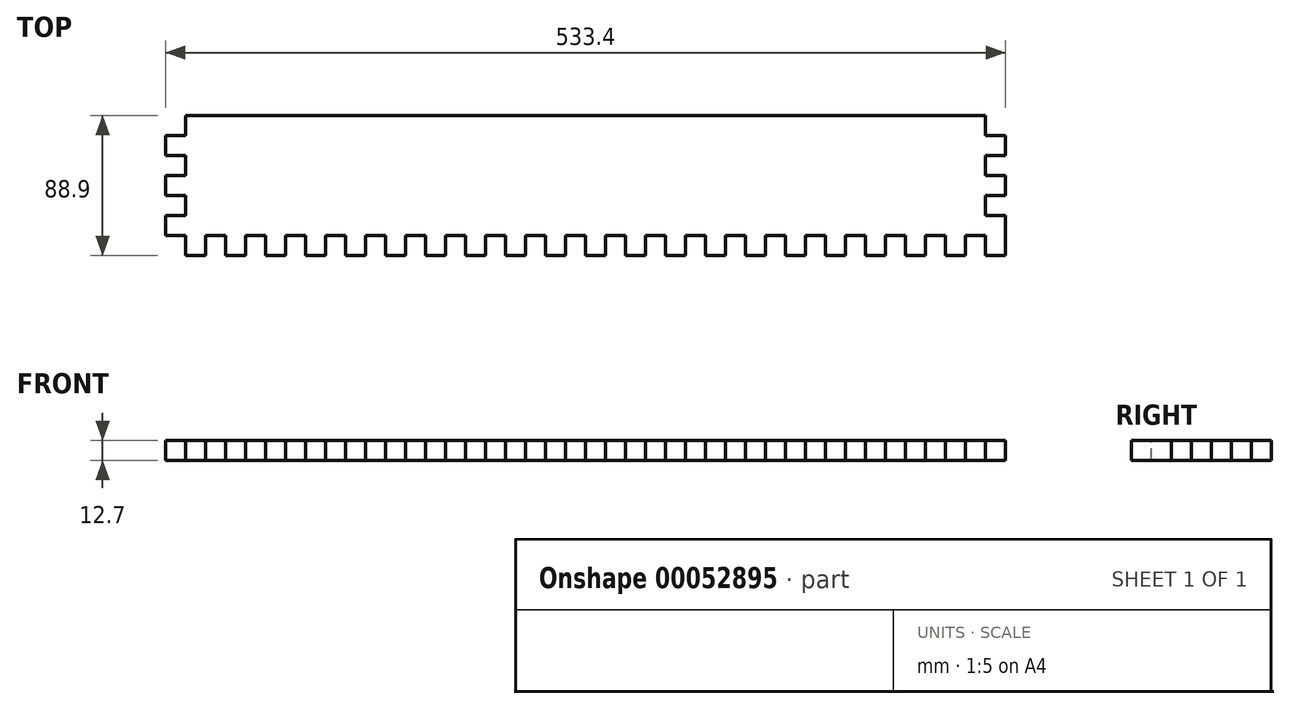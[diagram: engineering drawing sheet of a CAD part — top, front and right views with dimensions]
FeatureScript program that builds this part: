
annotation { "Feature Type Name" : "Feature", "Feature Type Description" : "" }
export const myFeature = defineFeature(function(context is Context, id is Id, definition is map)
    precondition{}
    {
        {
            var Q0;
            Q0=qCreatedBy(makeId("Top.planeOp"),FACE);
            var sketch = newSketch(context, id + "F0", { "sketchPlane" : qUnion([Q0])});
            skLineSegment(sketch, "E0.bottom", {"start": v(0, 0) * mm, "end": v(533.4, 0) * mm});
            skLineSegment(sketch, "E0.top", {"start": v(0, 88.9) * mm, "end": v(533.4, 88.9) * mm});
            skLineSegment(sketch, "E0.left", {"start": v(0, 0) * mm, "end": v(0, 88.9) * mm});
            skLineSegment(sketch, "E0.right", {"start": v(533.4, 0) * mm, "end": v(533.4, 88.9) * mm});
            skSolve(sketch);
        }
        {
            var Q0;
            Q0 = qSketchRegion(id + "F0", true);
            extrude(context, id + "F1", {"entities" : qUnion([Q0]), "depth" : 12.7 * mm});
        }
        {
            var Q0;
            Q0=makeQuery(id+"F1.opExtrude","CAP_FACE",FACE,{"disambiguationData":[OSD([sQuery(id+"F0.wireOp",EDGE,"E0.bottom"),sQuery(id+"F0.wireOp",EDGE,"E0.top"),sQuery(id+"F0.wireOp",EDGE,"E0.left"),sQuery(id+"F0.wireOp",EDGE,"E0.right")])],"isStart":false});
            var sketch = newSketch(context, id + "F2", { "sketchPlane" : qUnion([Q0])});
            skLineSegment(sketch, "E1.bottom", {"start": v(0, 0) * mm, "end": v(12.7, 0) * mm});
            skLineSegment(sketch, "E1.top", {"start": v(0, 12.7) * mm, "end": v(12.7, 12.7) * mm});
            skLineSegment(sketch, "E1.left", {"start": v(0, 0) * mm, "end": v(0, 12.7) * mm});
            skLineSegment(sketch, "E1.right", {"start": v(12.7, 0) * mm, "end": v(12.7, 12.7) * mm});
            skLineSegment(sketch, "E2.bottom", {"start": v(0, 25.4) * mm, "end": v(12.7, 25.4) * mm});
            skLineSegment(sketch, "E2.top", {"start": v(0, 38.1) * mm, "end": v(12.7, 38.1) * mm});
            skLineSegment(sketch, "E2.left", {"start": v(0, 25.4) * mm, "end": v(0, 38.1) * mm});
            skLineSegment(sketch, "E2.right", {"start": v(12.7, 25.4) * mm, "end": v(12.7, 38.1) * mm});
            skLineSegment(sketch, "E3.bottom", {"start": v(0, 76.2) * mm, "end": v(12.7, 76.2) * mm});
            skLineSegment(sketch, "E3.top", {"start": v(0, 88.9) * mm, "end": v(12.7, 88.9) * mm});
            skLineSegment(sketch, "E3.left", {"start": v(0, 76.2) * mm, "end": v(0, 88.9) * mm});
            skLineSegment(sketch, "E3.right", {"start": v(12.7, 76.2) * mm, "end": v(12.7, 88.9) * mm});
            skLineSegment(sketch, "E4.bottom", {"start": v(0, 50.8) * mm, "end": v(12.7, 50.8) * mm});
            skLineSegment(sketch, "E4.top", {"start": v(0, 63.5) * mm, "end": v(12.7, 63.5) * mm});
            skLineSegment(sketch, "E4.left", {"start": v(0, 50.8) * mm, "end": v(0, 63.5) * mm});
            skLineSegment(sketch, "E4.right", {"start": v(12.7, 50.8) * mm, "end": v(12.7, 63.5) * mm});
            skSolve(sketch);
        }
        {
            var Q0;
            Q0 = qSketchRegion(id + "F2", true);
            extrude(context, id + "F3", {"entities" : qUnion([Q0]), "operationType" : NewBodyOperationType.REMOVE, "oppositeDirection" : true, "depth" : 25.4 * mm});
        }
        {
            var Q0;
            Q0=makeQuery(id+"F1.opExtrude","CAP_FACE",FACE,{"disambiguationData":[OSD([sQuery(id+"F0.wireOp",EDGE,"E0.bottom"),sQuery(id+"F0.wireOp",EDGE,"E0.top"),sQuery(id+"F0.wireOp",EDGE,"E0.left"),sQuery(id+"F0.wireOp",EDGE,"E0.right")])],"isStart":false});
            var sketch = newSketch(context, id + "F4", { "sketchPlane" : qUnion([Q0])});
            skLineSegment(sketch, "E5.bottom", {"start": v(76.2, 0) * mm, "end": v(88.9, 0) * mm});
            skLineSegment(sketch, "E5.top", {"start": v(76.2, 12.7) * mm, "end": v(88.9, 12.7) * mm});
            skLineSegment(sketch, "E5.left", {"start": v(76.2, 0) * mm, "end": v(76.2, 12.7) * mm});
            skLineSegment(sketch, "E5.right", {"start": v(88.9, 0) * mm, "end": v(88.9, 12.7) * mm});
            skLineSegment(sketch, "E6.bottom", {"start": v(127, 0) * mm, "end": v(139.7, 0) * mm});
            skLineSegment(sketch, "E6.top", {"start": v(127, 12.7) * mm, "end": v(139.7, 12.7) * mm});
            skLineSegment(sketch, "E6.left", {"start": v(127, 0) * mm, "end": v(127, 12.7) * mm});
            skLineSegment(sketch, "E6.right", {"start": v(139.7, 0) * mm, "end": v(139.7, 12.7) * mm});
            skLineSegment(sketch, "E7.bottom", {"start": v(152.4, 0) * mm, "end": v(165.1, 0) * mm});
            skLineSegment(sketch, "E7.top", {"start": v(152.4, 12.7) * mm, "end": v(165.1, 12.7) * mm});
            skLineSegment(sketch, "E7.left", {"start": v(152.4, 0) * mm, "end": v(152.4, 12.7) * mm});
            skLineSegment(sketch, "E7.right", {"start": v(165.1, 0) * mm, "end": v(165.1, 12.7) * mm});
            skLineSegment(sketch, "E8.bottom", {"start": v(177.8, 0) * mm, "end": v(190.5, 0) * mm});
            skLineSegment(sketch, "E8.top", {"start": v(177.8, 12.7) * mm, "end": v(190.5, 12.7) * mm});
            skLineSegment(sketch, "E8.left", {"start": v(177.8, 0) * mm, "end": v(177.8, 12.7) * mm});
            skLineSegment(sketch, "E8.right", {"start": v(190.5, 0) * mm, "end": v(190.5, 12.7) * mm});
            skLineSegment(sketch, "E9.bottom", {"start": v(63.5, 0) * mm, "end": v(50.8, 0) * mm});
            skLineSegment(sketch, "E9.top", {"start": v(63.5, 12.7) * mm, "end": v(50.8, 12.7) * mm});
            skLineSegment(sketch, "E9.left", {"start": v(63.5, 0) * mm, "end": v(63.5, 12.7) * mm});
            skLineSegment(sketch, "E9.right", {"start": v(50.8, 0) * mm, "end": v(50.8, 12.7) * mm});
            skLineSegment(sketch, "E10.bottom", {"start": v(38.1, 0) * mm, "end": v(25.4, 0) * mm});
            skLineSegment(sketch, "E10.top", {"start": v(38.1, 12.7) * mm, "end": v(25.4, 12.7) * mm});
            skLineSegment(sketch, "E10.left", {"start": v(38.1, 0) * mm, "end": v(38.1, 12.7) * mm});
            skLineSegment(sketch, "E10.right", {"start": v(25.4, 0) * mm, "end": v(25.4, 12.7) * mm});
            skLineSegment(sketch, "E11.bottom", {"start": v(101.6, 0) * mm, "end": v(114.3, 0) * mm});
            skLineSegment(sketch, "E11.top", {"start": v(101.6, 12.7) * mm, "end": v(114.3, 12.7) * mm});
            skLineSegment(sketch, "E11.left", {"start": v(101.6, 0) * mm, "end": v(101.6, 12.7) * mm});
            skLineSegment(sketch, "E11.right", {"start": v(114.3, 0) * mm, "end": v(114.3, 12.7) * mm});
            skLineSegment(sketch, "E12.bottom", {"start": v(203.2, 0) * mm, "end": v(215.9, 0) * mm});
            skLineSegment(sketch, "E12.top", {"start": v(203.2, 12.7) * mm, "end": v(215.9, 12.7) * mm});
            skLineSegment(sketch, "E12.left", {"start": v(203.2, 0) * mm, "end": v(203.2, 12.7) * mm});
            skLineSegment(sketch, "E12.right", {"start": v(215.9, 0) * mm, "end": v(215.9, 12.7) * mm});
            skLineSegment(sketch, "E13.bottom", {"start": v(228.6, 0) * mm, "end": v(241.3, 0) * mm});
            skLineSegment(sketch, "E13.top", {"start": v(228.6, 12.7) * mm, "end": v(241.3, 12.7) * mm});
            skLineSegment(sketch, "E13.left", {"start": v(228.6, 0) * mm, "end": v(228.6, 12.7) * mm});
            skLineSegment(sketch, "E13.right", {"start": v(241.3, 0) * mm, "end": v(241.3, 12.7) * mm});
            skLineSegment(sketch, "E14.bottom", {"start": v(254, 0) * mm, "end": v(266.7, 0) * mm});
            skLineSegment(sketch, "E14.top", {"start": v(254, 12.7) * mm, "end": v(266.7, 12.7) * mm});
            skLineSegment(sketch, "E14.left", {"start": v(254, 0) * mm, "end": v(254, 12.7) * mm});
            skLineSegment(sketch, "E14.right", {"start": v(266.7, 0) * mm, "end": v(266.7, 12.7) * mm});
            skLineSegment(sketch, "E15.bottom", {"start": v(279.4, 0) * mm, "end": v(292.1, 0) * mm});
            skLineSegment(sketch, "E15.top", {"start": v(279.4, 12.7) * mm, "end": v(292.1, 12.7) * mm});
            skLineSegment(sketch, "E15.left", {"start": v(279.4, 0) * mm, "end": v(279.4, 12.7) * mm});
            skLineSegment(sketch, "E15.right", {"start": v(292.1, 0) * mm, "end": v(292.1, 12.7) * mm});
            skLineSegment(sketch, "E16.bottom", {"start": v(304.8, 0) * mm, "end": v(317.5, 0) * mm});
            skLineSegment(sketch, "E16.top", {"start": v(304.8, 12.7) * mm, "end": v(317.5, 12.7) * mm});
            skLineSegment(sketch, "E16.left", {"start": v(304.8, 0) * mm, "end": v(304.8, 12.7) * mm});
            skLineSegment(sketch, "E16.right", {"start": v(317.5, 0) * mm, "end": v(317.5, 12.7) * mm});
            skLineSegment(sketch, "E17.bottom", {"start": v(330.2, 0) * mm, "end": v(342.9, 0) * mm});
            skLineSegment(sketch, "E17.top", {"start": v(330.2, 12.7) * mm, "end": v(342.9, 12.7) * mm});
            skLineSegment(sketch, "E17.left", {"start": v(330.2, 0) * mm, "end": v(330.2, 12.7) * mm});
            skLineSegment(sketch, "E17.right", {"start": v(342.9, 0) * mm, "end": v(342.9, 12.7) * mm});
            skLineSegment(sketch, "E18.bottom", {"start": v(355.6, 0) * mm, "end": v(368.3, 0) * mm});
            skLineSegment(sketch, "E18.top", {"start": v(355.6, 12.7) * mm, "end": v(368.3, 12.7) * mm});
            skLineSegment(sketch, "E18.left", {"start": v(355.6, 0) * mm, "end": v(355.6, 12.7) * mm});
            skLineSegment(sketch, "E18.right", {"start": v(368.3, 0) * mm, "end": v(368.3, 12.7) * mm});
            skLineSegment(sketch, "E19.bottom", {"start": v(381, 0) * mm, "end": v(393.7, 0) * mm});
            skLineSegment(sketch, "E19.top", {"start": v(381, 12.7) * mm, "end": v(393.7, 12.7) * mm});
            skLineSegment(sketch, "E19.left", {"start": v(381, 0) * mm, "end": v(381, 12.7) * mm});
            skLineSegment(sketch, "E19.right", {"start": v(393.7, 0) * mm, "end": v(393.7, 12.7) * mm});
            skLineSegment(sketch, "E20.bottom", {"start": v(406.4, 0) * mm, "end": v(419.1, 0) * mm});
            skLineSegment(sketch, "E20.top", {"start": v(406.4, 12.7) * mm, "end": v(419.1, 12.7) * mm});
            skLineSegment(sketch, "E20.left", {"start": v(406.4, 0) * mm, "end": v(406.4, 12.7) * mm});
            skLineSegment(sketch, "E20.right", {"start": v(419.1, 0) * mm, "end": v(419.1, 12.7) * mm});
            skLineSegment(sketch, "E21.bottom", {"start": v(431.8, 0) * mm, "end": v(444.5, 0) * mm});
            skLineSegment(sketch, "E21.top", {"start": v(431.8, 12.7) * mm, "end": v(444.5, 12.7) * mm});
            skLineSegment(sketch, "E21.left", {"start": v(431.8, 0) * mm, "end": v(431.8, 12.7) * mm});
            skLineSegment(sketch, "E21.right", {"start": v(444.5, 0) * mm, "end": v(444.5, 12.7) * mm});
            skLineSegment(sketch, "E22.bottom", {"start": v(457.2, 0) * mm, "end": v(469.9, 0) * mm});
            skLineSegment(sketch, "E22.top", {"start": v(457.2, 12.7) * mm, "end": v(469.9, 12.7) * mm});
            skLineSegment(sketch, "E22.left", {"start": v(457.2, 0) * mm, "end": v(457.2, 12.7) * mm});
            skLineSegment(sketch, "E22.right", {"start": v(469.9, 0) * mm, "end": v(469.9, 12.7) * mm});
            skLineSegment(sketch, "E23.bottom", {"start": v(482.6, 0) * mm, "end": v(495.3, 0) * mm});
            skLineSegment(sketch, "E23.top", {"start": v(482.6, 12.7) * mm, "end": v(495.3, 12.7) * mm});
            skLineSegment(sketch, "E23.left", {"start": v(482.6, 0) * mm, "end": v(482.6, 12.7) * mm});
            skLineSegment(sketch, "E23.right", {"start": v(495.3, 0) * mm, "end": v(495.3, 12.7) * mm});
            skLineSegment(sketch, "E24.bottom", {"start": v(508, 0) * mm, "end": v(520.7, 0) * mm});
            skLineSegment(sketch, "E24.top", {"start": v(508, 12.7) * mm, "end": v(520.7, 12.7) * mm});
            skLineSegment(sketch, "E24.left", {"start": v(508, 0) * mm, "end": v(508, 12.7) * mm});
            skLineSegment(sketch, "E24.right", {"start": v(520.7, 0) * mm, "end": v(520.7, 12.7) * mm});
            skSolve(sketch);
        }
        {
            var Q0;
            Q0 = qSketchRegion(id + "F4", true);
            extrude(context, id + "F5", {"entities" : qUnion([Q0]), "operationType" : NewBodyOperationType.REMOVE, "oppositeDirection" : true, "depth" : 25.4 * mm});
        }
        {
            var Q0;
            Q0=makeQuery(id+"F1.opExtrude","CAP_FACE",FACE,{"disambiguationData":[OSD([sQuery(id+"F0.wireOp",EDGE,"E0.bottom"),sQuery(id+"F0.wireOp",EDGE,"E0.top"),sQuery(id+"F0.wireOp",EDGE,"E0.left"),sQuery(id+"F0.wireOp",EDGE,"E0.right")])],"isStart":false});
            var sketch = newSketch(context, id + "F6", { "sketchPlane" : qUnion([Q0])});
            skLineSegment(sketch, "E25.bottom", {"start": v(533.4, 88.9) * mm, "end": v(520.7, 88.9) * mm});
            skLineSegment(sketch, "E25.top", {"start": v(533.4, 76.2) * mm, "end": v(520.7, 76.2) * mm});
            skLineSegment(sketch, "E25.left", {"start": v(533.4, 88.9) * mm, "end": v(533.4, 76.2) * mm});
            skLineSegment(sketch, "E25.right", {"start": v(520.7, 88.9) * mm, "end": v(520.7, 76.2) * mm});
            skLineSegment(sketch, "E26.bottom", {"start": v(533.4, 63.5) * mm, "end": v(520.7, 63.5) * mm});
            skLineSegment(sketch, "E26.top", {"start": v(533.4, 50.8) * mm, "end": v(520.7, 50.8) * mm});
            skLineSegment(sketch, "E26.left", {"start": v(533.4, 63.5) * mm, "end": v(533.4, 50.8) * mm});
            skLineSegment(sketch, "E26.right", {"start": v(520.7, 63.5) * mm, "end": v(520.7, 50.8) * mm});
            skLineSegment(sketch, "E27.bottom", {"start": v(533.4, 38.1) * mm, "end": v(520.7, 38.1) * mm});
            skLineSegment(sketch, "E27.top", {"start": v(533.4, 25.4) * mm, "end": v(520.7, 25.4) * mm});
            skLineSegment(sketch, "E27.left", {"start": v(533.4, 38.1) * mm, "end": v(533.4, 25.4) * mm});
            skLineSegment(sketch, "E27.right", {"start": v(520.7, 38.1) * mm, "end": v(520.7, 25.4) * mm});
            skSolve(sketch);
        }
        {
            var Q0;
            Q0 = qSketchRegion(id + "F6", true);
            extrude(context, id + "F7", {"entities" : qUnion([Q0]), "operationType" : NewBodyOperationType.REMOVE, "oppositeDirection" : true, "depth" : 25.4 * mm});
        }
    });
